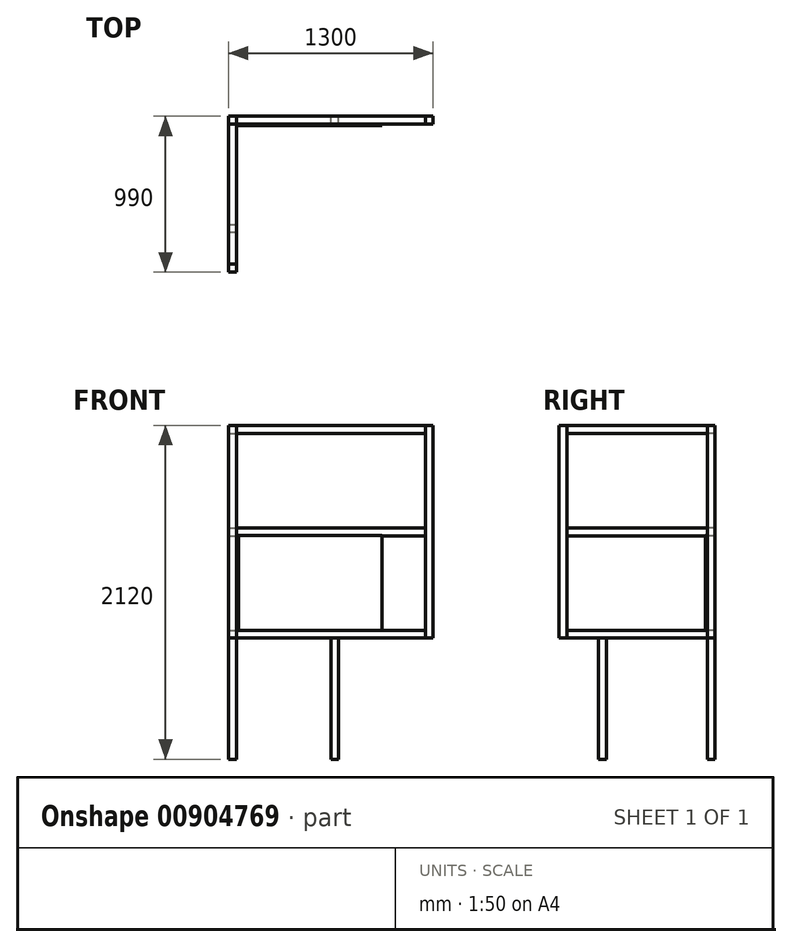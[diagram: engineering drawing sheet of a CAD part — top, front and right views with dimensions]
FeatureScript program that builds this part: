
annotation { "Feature Type Name" : "Feature", "Feature Type Description" : "" }
export const myFeature = defineFeature(function(context is Context, id is Id, definition is map)
    precondition{}
    {
        {
            var Q0;
            Q0=qCreatedBy(makeId("Top.planeOp"),FACE);
            var sketch = newSketch(context, id + "F0", { "sketchPlane" : qUnion([Q0])});
            skLineSegment(sketch, "E0.bottom", {"start": v(25, 25) * mm, "end": v(-25, 25) * mm});
            skLineSegment(sketch, "E0.top", {"start": v(25, -25) * mm, "end": v(-25, -25) * mm});
            skLineSegment(sketch, "E0.left", {"start": v(25, 25) * mm, "end": v(25, -25) * mm});
            skLineSegment(sketch, "E0.right", {"start": v(-25, 25) * mm, "end": v(-25, -25) * mm});
            skPoint(sketch, "E0.middle", {"position": v(0, 0) * mm});
            skSolve(sketch);
        }
        {
            var Q0;
            Q0 = qSketchRegion(id + "F0", true);
            extrude(context, id + "F1", {"entities" : qUnion([Q0]), "depth" : 2120 * mm, "offsetDistance" : 25 * mm});
        }
        {
            var Q0;
            Q0=makeQuery(id+"F1.opExtrude","SWEPT_FACE",FACE,{"disambiguationData":[OSD([sQuery(id+"F0.wireOp",EDGE,"E0.top")])]});
            var sketch = newSketch(context, id + "F2", { "sketchPlane" : qUnion([Q0])});
            skLineSegment(sketch, "E1.bottom", {"start": v(-25, 2120) * mm, "end": v(25, 2120) * mm});
            skLineSegment(sketch, "E1.top", {"start": v(-25, 2070) * mm, "end": v(25, 2070) * mm});
            skLineSegment(sketch, "E1.left", {"start": v(-25, 2120) * mm, "end": v(-25, 2070) * mm});
            skLineSegment(sketch, "E1.right", {"start": v(25, 2120) * mm, "end": v(25, 2070) * mm});
            skSolve(sketch);
        }
        {
            var Q0;
            Q0 = qSketchRegion(id + "F2", true);
            extrude(context, id + "F3", {"entities" : qUnion([Q0]), "depth" : 890 * mm, "offsetDistance" : 25 * mm});
        }
        {
            var Q0;
            Q0=makeQuery(id+"F3.opExtrude","SWEPT_FACE",FACE,{"disambiguationData":[OSD([sQuery(id+"F2.wireOp",EDGE,"E1.bottom")])]});
            var sketch = newSketch(context, id + "F4", { "sketchPlane" : qUnion([Q0])});
            skLineSegment(sketch, "E2.bottom", {"start": v(-25, -915) * mm, "end": v(25, -915) * mm});
            skLineSegment(sketch, "E2.top", {"start": v(-25, -965) * mm, "end": v(25, -965) * mm});
            skLineSegment(sketch, "E2.left", {"start": v(-25, -915) * mm, "end": v(-25, -965) * mm});
            skLineSegment(sketch, "E2.right", {"start": v(25, -915) * mm, "end": v(25, -965) * mm});
            skSolve(sketch);
        }
        {
            var Q0;
            Q0 = qSketchRegion(id + "F4", true);
            extrude(context, id + "F5", {"entities" : qUnion([Q0]), "oppositeDirection" : true, "depth" : 1350 * mm, "offsetDistance" : 25 * mm});
        }
        {
            var Q0;
            Q0=makeQuery(id+"F5.opExtrude","SWEPT_FACE",FACE,{"disambiguationData":[OSD([sQuery(id+"F4.wireOp",EDGE,"E2.bottom")])]});
            var sketch = newSketch(context, id + "F6", { "sketchPlane" : qUnion([Q0])});
            skLineSegment(sketch, "E3.bottom", {"start": v(-25, 770) * mm, "end": v(25, 770) * mm});
            skLineSegment(sketch, "E3.top", {"start": v(-25, 820) * mm, "end": v(25, 820) * mm});
            skLineSegment(sketch, "E3.left", {"start": v(-25, 770) * mm, "end": v(-25, 820) * mm});
            skLineSegment(sketch, "E3.right", {"start": v(25, 770) * mm, "end": v(25, 820) * mm});
            skSolve(sketch);
        }
        {
            var Q0;
            Q0 = qSketchRegion(id + "F6", true);
            var Q1;
            Q1=makeQuery(id+"F1.opExtrude","SWEPT_FACE",FACE,{"disambiguationData":[OSD([sQuery(id+"F0.wireOp",EDGE,"E0.top")])]});
            extrude(context, id + "F7", {"entities" : qUnion([Q0]), "endBound" : BoundingType.UP_TO_SURFACE, "depth" : 25 * mm, "endBoundEntityFace" : qUnion([Q1]), "offsetDistance" : 25 * mm});
        }
        {
            var Q0;
            Q0=makeQuery(id+"F1.opExtrude","SWEPT_FACE",FACE,{"disambiguationData":[OSD([sQuery(id+"F0.wireOp",EDGE,"E0.left")])]});
            var sketch = newSketch(context, id + "F8", { "sketchPlane" : qUnion([Q0])});
            skLineSegment(sketch, "E4.bottom", {"start": v(25, 2120) * mm, "end": v(-25, 2120) * mm});
            skLineSegment(sketch, "E4.top", {"start": v(25, 2070) * mm, "end": v(-25, 2070) * mm});
            skLineSegment(sketch, "E4.left", {"start": v(25, 2120) * mm, "end": v(25, 2070) * mm});
            skLineSegment(sketch, "E4.right", {"start": v(-25, 2120) * mm, "end": v(-25, 2070) * mm});
            skSolve(sketch);
        }
        {
            var Q0;
            Q0 = qSketchRegion(id + "F8", true);
            extrude(context, id + "F9", {"entities" : qUnion([Q0]), "depth" : 1200 * mm, "offsetDistance" : 25 * mm});
        }
        {
            var Q0;
            Q0=makeQuery(id+"F9.opExtrude","SWEPT_FACE",FACE,{"disambiguationData":[OSD([sQuery(id+"F8.wireOp",EDGE,"E4.bottom")])]});
            var sketch = newSketch(context, id + "F10", { "sketchPlane" : qUnion([Q0])});
            skLineSegment(sketch, "E5.bottom", {"start": v(1225, -25) * mm, "end": v(1275, -25) * mm});
            skLineSegment(sketch, "E5.top", {"start": v(1225, 25) * mm, "end": v(1275, 25) * mm});
            skLineSegment(sketch, "E5.left", {"start": v(1225, -25) * mm, "end": v(1225, 25) * mm});
            skLineSegment(sketch, "E5.right", {"start": v(1275, -25) * mm, "end": v(1275, 25) * mm});
            skSolve(sketch);
        }
        {
            var Q0;
            Q0 = qSketchRegion(id + "F10", true);
            var Q1;
            Q1=makeQuery(id+"F7.opExtrude","SWEPT_FACE",FACE,{"disambiguationData":[OSD([sQuery(id+"F6.wireOp",EDGE,"E3.bottom")])]});
            extrude(context, id + "F11", {"entities" : qUnion([Q0]), "endBound" : BoundingType.UP_TO_SURFACE, "oppositeDirection" : true, "depth" : 25 * mm, "endBoundEntityFace" : qUnion([Q1]), "offsetDistance" : 25 * mm});
        }
        {
            var Q0;
            Q0=makeQuery(id+"F1.opExtrude","SWEPT_FACE",FACE,{"disambiguationData":[OSD([sQuery(id+"F0.wireOp",EDGE,"E0.left")])]});
            var sketch = newSketch(context, id + "F12", { "sketchPlane" : qUnion([Q0])});
            skLineSegment(sketch, "E6.bottom", {"start": v(-25, 770) * mm, "end": v(25, 770) * mm});
            skLineSegment(sketch, "E6.top", {"start": v(-25, 820) * mm, "end": v(25, 820) * mm});
            skLineSegment(sketch, "E6.left", {"start": v(-25, 770) * mm, "end": v(-25, 820) * mm});
            skLineSegment(sketch, "E6.right", {"start": v(25, 770) * mm, "end": v(25, 820) * mm});
            skSolve(sketch);
        }
        {
            var Q0;
            Q0 = qSketchRegion(id + "F12", true);
            var Q1;
            Q1=makeQuery(id+"F11.opExtrude","SWEPT_FACE",FACE,{"disambiguationData":[OSD([sQuery(id+"F10.wireOp",EDGE,"E5.left")])]});
            extrude(context, id + "F13", {"entities" : qUnion([Q0]), "endBound" : BoundingType.UP_TO_SURFACE, "depth" : 25 * mm, "endBoundEntityFace" : qUnion([Q1]), "offsetDistance" : 25 * mm});
        }
        {
            var Q0;
            Q0=makeQuery(id+"F7.opExtrude","SWEPT_FACE",FACE,{"disambiguationData":[OSD([sQuery(id+"F6.wireOp",EDGE,"E3.bottom")])]});
            var sketch = newSketch(context, id + "F14", { "sketchPlane" : qUnion([Q0])});
            skLineSegment(sketch, "E7.bottom", {"start": v(-25, 715) * mm, "end": v(25, 715) * mm});
            skLineSegment(sketch, "E7.top", {"start": v(-25, 665) * mm, "end": v(25, 665) * mm});
            skLineSegment(sketch, "E7.left", {"start": v(-25, 715) * mm, "end": v(-25, 665) * mm});
            skLineSegment(sketch, "E7.right", {"start": v(25, 715) * mm, "end": v(25, 665) * mm});
            skSolve(sketch);
        }
        {
            var Q0;
            Q0 = qSketchRegion(id + "F14", true);
            var Q1;
            Q1=makeQuery(id+"F1.opExtrude","CAP_FACE",FACE,{"disambiguationData":[OSD([sQuery(id+"F0.wireOp",EDGE,"E0.bottom"),sQuery(id+"F0.wireOp",EDGE,"E0.top"),sQuery(id+"F0.wireOp",EDGE,"E0.left"),sQuery(id+"F0.wireOp",EDGE,"E0.right")])],"isStart":true});
            extrude(context, id + "F15", {"entities" : qUnion([Q0]), "endBound" : BoundingType.UP_TO_SURFACE, "depth" : 25 * mm, "endBoundEntityFace" : qUnion([Q1]), "offsetDistance" : 25 * mm});
        }
        {
            var Q0;
            Q0=makeQuery(id+"F1.opExtrude","SWEPT_FACE",FACE,{"disambiguationData":[OSD([sQuery(id+"F0.wireOp",EDGE,"E0.left")])]});
            var sketch = newSketch(context, id + "F16", { "sketchPlane" : qUnion([Q0])});
            skLineSegment(sketch, "E8.bottom", {"start": v(-25, 1420) * mm, "end": v(25, 1420) * mm});
            skLineSegment(sketch, "E8.top", {"start": v(-25, 1470) * mm, "end": v(25, 1470) * mm});
            skLineSegment(sketch, "E8.left", {"start": v(-25, 1420) * mm, "end": v(-25, 1470) * mm});
            skLineSegment(sketch, "E8.right", {"start": v(25, 1420) * mm, "end": v(25, 1470) * mm});
            skLineSegment(sketch, "E9", {"start": v(25, 1470) * mm, "end": v(-25, 1420) * mm, "construction": true});
            skLineSegment(sketch, "E10", {"start": v(0, 820) * mm, "end": v(0, 2070) * mm, "construction": true});
            skPoint(sketch, "E11", {"position": v(0, 1445) * mm});
            skSolve(sketch);
        }
        {
            var Q0;
            Q0 = qSketchRegion(id + "F16", true);
            var Q1;
            Q1=makeQuery(id+"F11.opExtrude","SWEPT_FACE",FACE,{"disambiguationData":[OSD([sQuery(id+"F10.wireOp",EDGE,"E5.left")])]});
            extrude(context, id + "F17", {"entities" : qUnion([Q0]), "endBound" : BoundingType.UP_TO_SURFACE, "depth" : 25 * mm, "endBoundEntityFace" : qUnion([Q1]), "offsetDistance" : 25 * mm});
        }
        {
            var Q0;
            Q0=makeQuery(id+"F1.opExtrude","SWEPT_FACE",FACE,{"disambiguationData":[OSD([sQuery(id+"F0.wireOp",EDGE,"E0.top")])]});
            var sketch = newSketch(context, id + "F18", { "sketchPlane" : qUnion([Q0])});
            skLineSegment(sketch, "E12.bottom", {"start": v(25, 1470) * mm, "end": v(-25, 1470) * mm});
            skLineSegment(sketch, "E12.top", {"start": v(25, 1420) * mm, "end": v(-25, 1420) * mm});
            skLineSegment(sketch, "E12.left", {"start": v(25, 1470) * mm, "end": v(25, 1420) * mm});
            skLineSegment(sketch, "E12.right", {"start": v(-25, 1470) * mm, "end": v(-25, 1420) * mm});
            skSolve(sketch);
        }
        {
            var Q0;
            Q0 = qSketchRegion(id + "F18", true);
            var Q1;
            Q1=makeQuery(id+"F5.opExtrude","SWEPT_FACE",FACE,{"disambiguationData":[OSD([sQuery(id+"F4.wireOp",EDGE,"E2.bottom")])]});
            extrude(context, id + "F19", {"entities" : qUnion([Q0]), "endBound" : BoundingType.UP_TO_SURFACE, "depth" : 25 * mm, "endBoundEntityFace" : qUnion([Q1]), "offsetDistance" : 25 * mm});
        }
        {
            var Q0;
            Q0=makeQuery(id+"F17.opExtrude","SWEPT_FACE",FACE,{"disambiguationData":[OSD([sQuery(id+"F16.wireOp",EDGE,"E8.left")])]});
            var sketch = newSketch(context, id + "F20", { "sketchPlane" : qUnion([Q0])});
            skLineSegment(sketch, "E13.bottom", {"start": v(38.64, 817.5) * mm, "end": v(948.64, 817.5) * mm});
            skLineSegment(sketch, "E13.top", {"start": v(38.64, 1422.5) * mm, "end": v(948.64, 1422.5) * mm});
            skLineSegment(sketch, "E13.left", {"start": v(38.64, 817.5) * mm, "end": v(38.64, 1422.5) * mm});
            skLineSegment(sketch, "E13.right", {"start": v(948.64, 817.5) * mm, "end": v(948.64, 1422.5) * mm});
            skSolve(sketch);
        }
        {
            var Q0;
            Q0 = qSketchRegion(id + "F20", true);
            extrude(context, id + "F21", {"entities" : qUnion([Q0]), "depth" : 10 * mm, "offsetDistance" : 25 * mm});
        }
        {
            var Q0;
            Q0=makeQuery(id+"F13.opExtrude","SWEPT_FACE",FACE,{"disambiguationData":[OSD([sQuery(id+"F12.wireOp",EDGE,"E6.bottom")])]});
            var sketch = newSketch(context, id + "F22", { "sketchPlane" : qUnion([Q0])});
            skLineSegment(sketch, "E14.bottom", {"start": v(675, -25) * mm, "end": v(625, -25) * mm});
            skLineSegment(sketch, "E14.top", {"start": v(675, 25) * mm, "end": v(625, 25) * mm});
            skLineSegment(sketch, "E14.left", {"start": v(675, -25) * mm, "end": v(675, 25) * mm});
            skLineSegment(sketch, "E14.right", {"start": v(625, -25) * mm, "end": v(625, 25) * mm});
            skSolve(sketch);
        }
        {
            var Q0;
            Q0 = qSketchRegion(id + "F22", true);
            var Q1;
            Q1=makeQuery(id+"F1.opExtrude","CAP_FACE",FACE,{"disambiguationData":[OSD([sQuery(id+"F0.wireOp",EDGE,"E0.bottom"),sQuery(id+"F0.wireOp",EDGE,"E0.top"),sQuery(id+"F0.wireOp",EDGE,"E0.left"),sQuery(id+"F0.wireOp",EDGE,"E0.right")])],"isStart":true});
            extrude(context, id + "F23", {"entities" : qUnion([Q0]), "endBound" : BoundingType.UP_TO_SURFACE, "depth" : 25 * mm, "endBoundEntityFace" : qUnion([Q1]), "offsetDistance" : 25 * mm});
        }
    });
